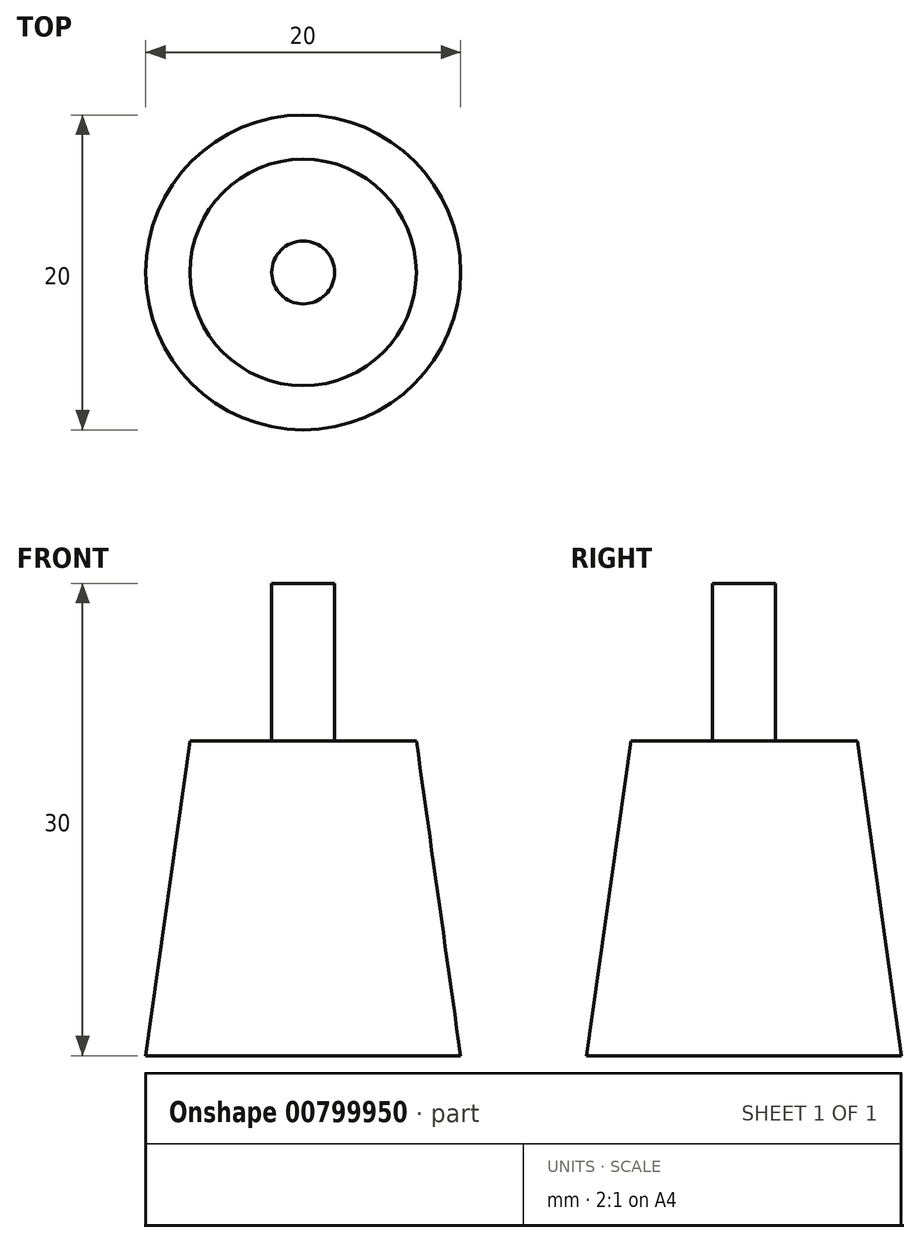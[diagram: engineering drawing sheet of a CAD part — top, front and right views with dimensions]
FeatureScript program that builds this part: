
annotation { "Feature Type Name" : "Feature", "Feature Type Description" : "" }
export const myFeature = defineFeature(function(context is Context, id is Id, definition is map)
    precondition{}
    {
        {
            var Q0;
            Q0=qCreatedBy(makeId("Top.planeOp"),FACE);
            var sketch = newSketch(context, id + "F0", { "sketchPlane" : qUnion([Q0])});
            skCircle(sketch, "E0", {"center": v(0, 0) * mm, "radius": 10 * mm});
            skSolve(sketch);
        }
        {
            var Q0;
            Q0=makeQuery(id+"F0.imprint","IMPRINT",FACE,{"disambiguationData":[TD([[makeQuery(id+"F0.imprint","IMPRINT",EDGE,{"derivedFrom":sQuery(id+"F0.wireOp",EDGE,"E0")}),1.0]])]});
            var Q1;
            Q1=sQuery(id+"F0.wireOp",EDGE,"E0");
            extrude(context, id + "F1", {"entities" : qUnion([Q0]), "surfaceEntities" : qUnion([Q1]), "depth" : 20 * mm, "offsetDistance" : 25 * mm, "hasDraft" : true, "draftAngle" : 8 * degree, "draftPullDirection" : true});
        }
        {
            var Q0;
            Q0=makeQuery(id+"F1.opExtrude","CAP_FACE",FACE,{"disambiguationData":[OSD([sQuery(id+"F0.wireOp",EDGE,"E0")])],"isStart":false});
            var sketch = newSketch(context, id + "F2", { "sketchPlane" : qUnion([Q0])});
            skCircle(sketch, "E1", {"center": v(0, 0) * mm, "radius": 2 * mm});
            skSolve(sketch);
        }
        {
            var Q0;
            Q0=makeQuery(id+"F2.imprint","IMPRINT",FACE,{"disambiguationData":[TD([[makeQuery(id+"F2.imprint","IMPRINT",EDGE,{"derivedFrom":sQuery(id+"F2.wireOp",EDGE,"E1")}),1.0]])]});
            extrude(context, id + "F3", {"entities" : qUnion([Q0]), "operationType" : NewBodyOperationType.ADD, "depth" : 10 * mm, "offsetDistance" : 25 * mm});
        }
    });
